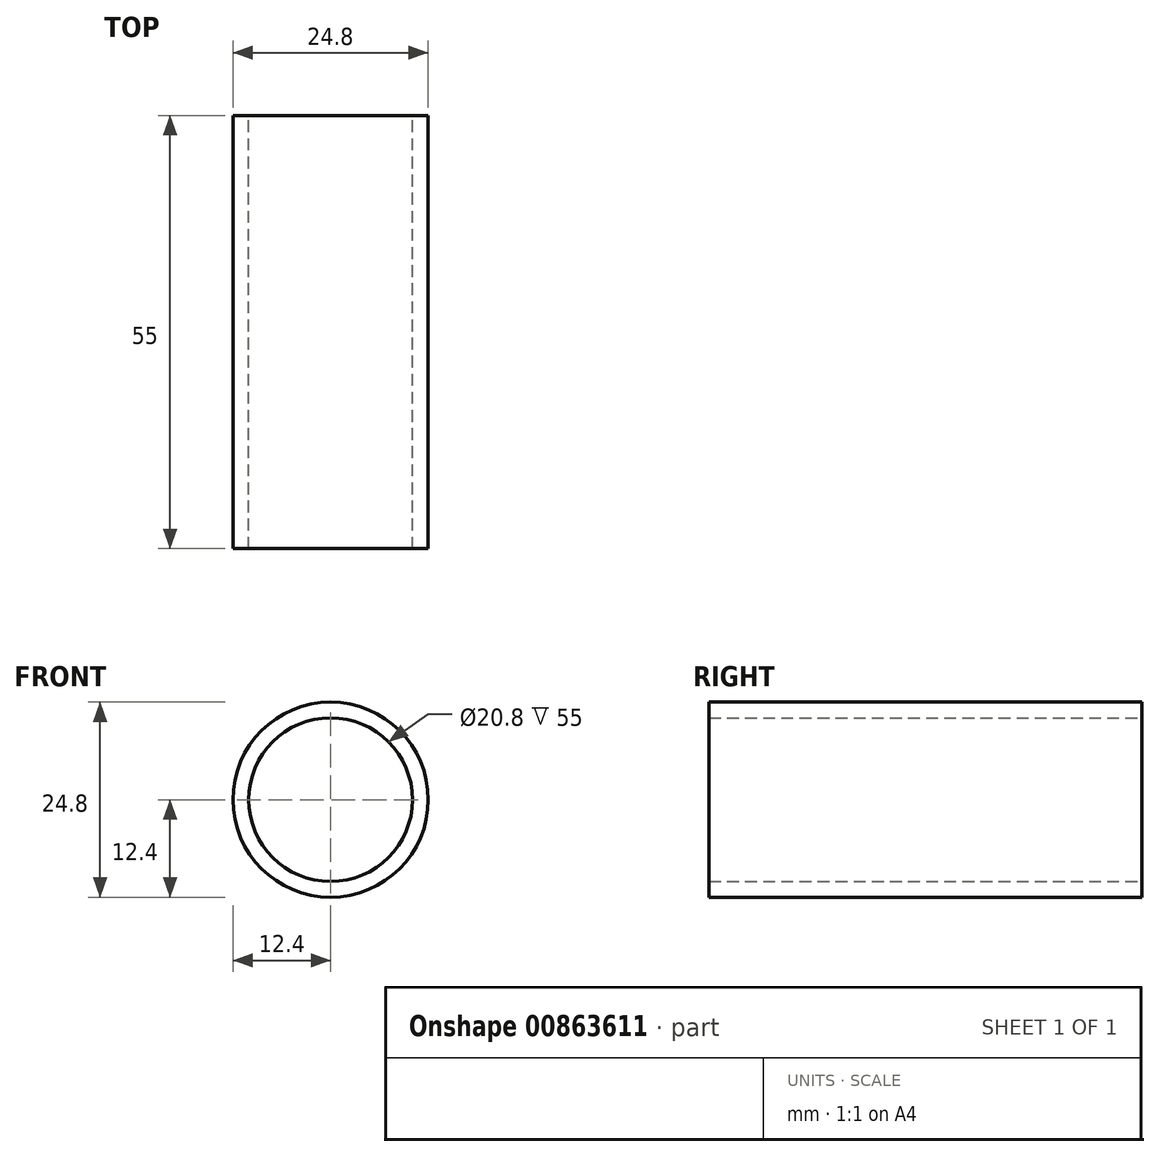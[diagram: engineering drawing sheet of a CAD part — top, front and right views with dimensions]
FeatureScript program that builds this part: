
annotation { "Feature Type Name" : "Feature", "Feature Type Description" : "" }
export const myFeature = defineFeature(function(context is Context, id is Id, definition is map)
    precondition{}
    {
        {
            var Q0;
            Q0=qCreatedBy(makeId("Front.planeOp"),FACE);
            var sketch = newSketch(context, id + "F0", { "sketchPlane" : qUnion([Q0])});
            skLineSegment(sketch, "E0", {"start": v(46.2, 24.2) * mm, "end": v(46.2, -23.33) * mm});
            skCircle(sketch, "E1", {"center": v(0, 0) * mm, "radius": 12.4 * mm});
            skCircle(sketch, "E2", {"center": v(0, 0) * mm, "radius": 10.4 * mm});
            skSolve(sketch);
        }
        {
            var Q0;
            Q0 = qSketchRegion(id + "F0", true);
            extrude(context, id + "F1", {"entities" : qUnion([Q0]), "depth" : 55 * mm, "offsetDistance" : 25.4 * mm});
        }
    });
